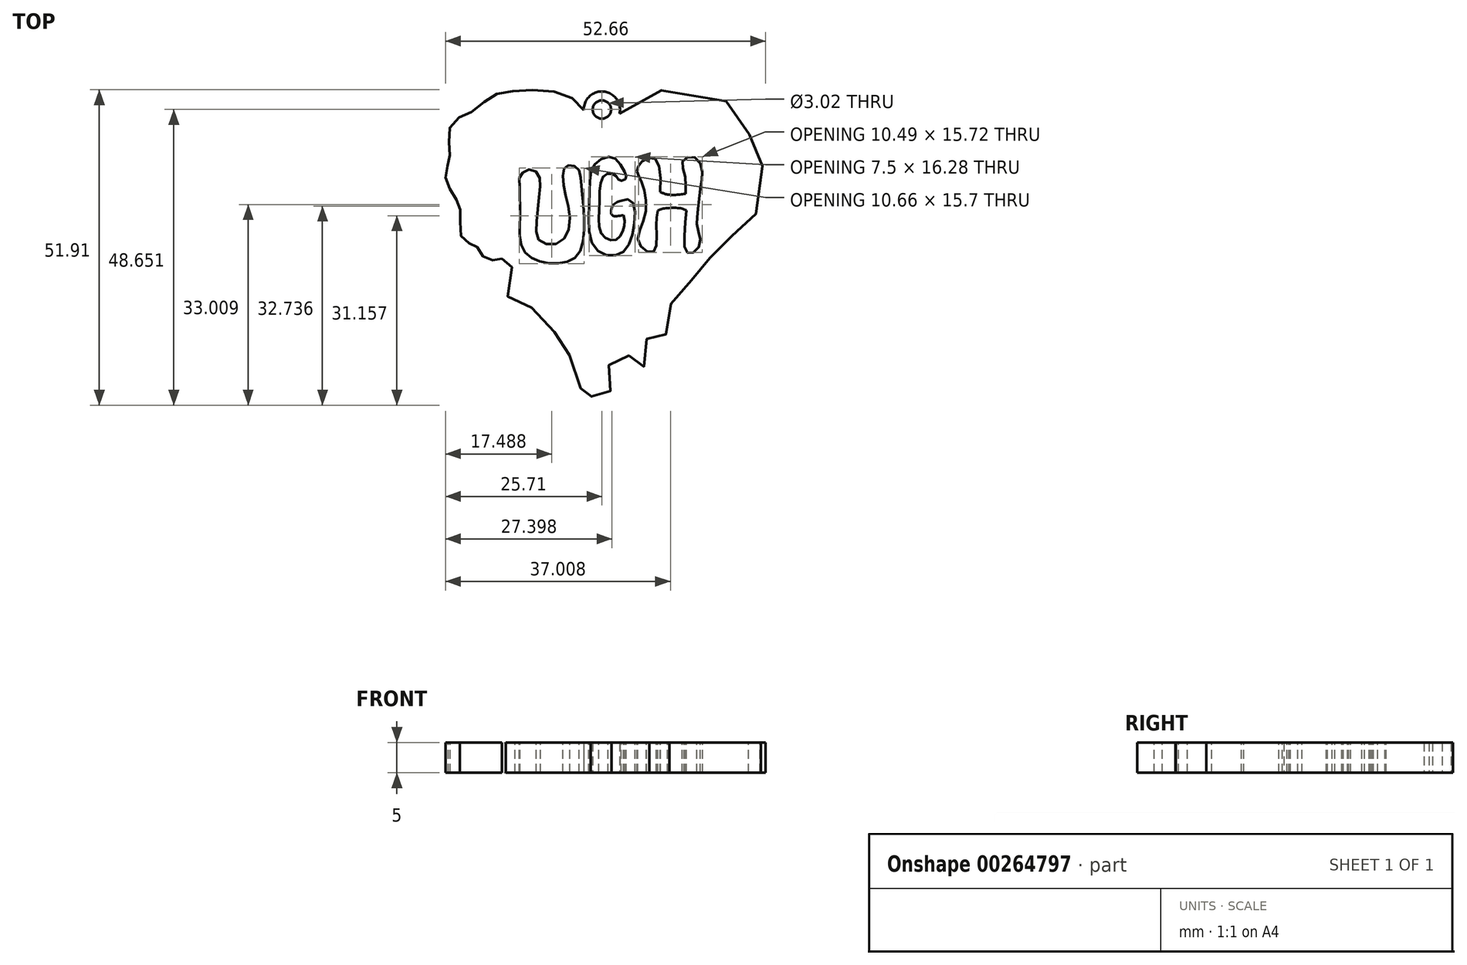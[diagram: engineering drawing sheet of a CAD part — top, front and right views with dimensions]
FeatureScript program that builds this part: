
annotation { "Feature Type Name" : "Feature", "Feature Type Description" : "" }
export const myFeature = defineFeature(function(context is Context, id is Id, definition is map)
    precondition{}
    {
        {
            var Q0;
            Q0=qCreatedBy(makeId("Top.planeOp"),FACE);
            var sketch = newSketch(context, id + "F0", { "sketchPlane" : qUnion([Q0])});
            skLineSegment(sketch, "E0", {"start": v(0.08, 15.96) * mm, "end": v(0.08, -29.04) * mm, "construction": true});
            skFitSpline(sketch, "E1", {"points": [v(0.08, 15.12) * mm, v(1.8, 15.96) * mm, v(5.58, 18.64) * mm, v(10.27, 20.57) * mm, v(19.75, 18.98) * mm, v(24.03, 15.96) * mm, v(24.45, 12.86) * mm, v(26.8, 11.1) * mm, v(26.13, 6.82) * mm, v(26.04, 2.12) * mm, v(23.27, -2.16) * mm, v(21.76, -2.5) * mm, v(21.1, -4.34) * mm, v(19.08, -6.1) * mm, v(17.82, -6.94) * mm, v(17.4, -9.03) * mm, v(15.64, -10.54) * mm, v(14.05, -10.96) * mm, v(13.55, -11.97) * mm, v(11.31, -14.7) * mm, v(10.84, -16.77) * mm, v(11.02, -19.08) * mm, v(9.42, -19.91) * mm, v(8.4, -19.08) * mm, v(7.52, -19.68) * mm, v(7.64, -22.23) * mm, v(7.7, -24.18) * mm, v(6.92, -24.96) * mm, v(6.21, -24.54) * mm, v(5.98, -25.01) * mm, v(5.09, -23.65) * mm, v(3.95, -23.12) * mm, v(3.15, -23.83) * mm, v(2.05, -24.06) * mm, v(1.07, -24.92) * mm, v(1.37, -27.18) * mm, v(1.6, -28.22) * mm, v(1.31, -29.31) * mm, v(0.68, -31) * mm, v(-1.46, -30.7) * mm, v(-1.93, -27.26) * mm, v(-2.64, -27.61) * mm, v(-3.35, -28.5) * mm, v(-4.3, -27.67) * mm, v(-5.2, -23.88) * mm, v(-5.67, -22.34) * mm, v(-6.74, -20.85) * mm, v(-7.62, -19.37) * mm, v(-10.41, -18.13) * mm, v(-11.48, -16) * mm, v(-12.13, -13.86) * mm, v(-14.5, -14.15) * mm, v(-15.75, -12.61) * mm, v(-15.51, -9.65) * mm, v(-15.04, -9) * mm, v(-14.33, -7.33) * mm, v(-14.5, -6.15) * mm, v(-16.46, -7.15) * mm], "startDerivative": vector(95.52, 38.59) * mm, "endDerivative": vector(-155.6, -97.2) * mm});
            skFitSpline(sketch, "E2", {"points": [v(-16.46, -7.15) * mm, v(-17.56, -7.42) * mm, v(-19.07, -7.15) * mm, v(-20.23, -5.85) * mm, v(-20.94, -4.84) * mm, v(-22.37, -4.47) * mm, v(-23.32, -2.82) * mm, v(-23.25, 0) * mm, v(-23.46, 1.56) * mm, v(-24.38, 3.32) * mm, v(-25.54, 5.33) * mm, v(-25.65, 7.1) * mm, v(-25.15, 9) * mm, v(-24.98, 10.83) * mm, v(-25.19, 13.83) * mm, v(-23.58, 15.97) * mm, v(-21.2, 17.06) * mm, v(-18.3, 19.45) * mm, v(-15.24, 20.33) * mm, v(-9.5, 20.5) * mm, v(-4.33, 18.86) * mm, v(-2.15, 16.14) * mm, v(-0.7, 15.1) * mm, v(0.08, 15.12) * mm], "startDerivative": vector(-33.79, -11.1) * mm, "endDerivative": vector(28.69, 5.55) * mm});
            skFitSpline(sketch, "E3", {"points": [v(-15.54, 7.18) * mm, v(-16.93, 6.43) * mm, v(-18.22, 6.03) * mm, v(-18.97, 4.49) * mm, v(-17.48, 2.5) * mm, v(-15.18, 1.6) * mm, v(-13.54, 0) * mm, v(-10.45, 0) * mm, v(-8.2, 0.55) * mm, v(-7.81, 0.5) * mm, v(-7.52, 0.56) * mm, v(-7.36, 1.37) * mm, v(-6.93, 1.67) * mm, v(-6.3, 2.5) * mm, v(-5.9, 2.96) * mm, v(-5.21, 3.13) * mm, v(-3.7, 4.49) * mm, v(-3.46, 7.08) * mm, v(-3.3, 9.72) * mm, v(-4.6, 11.37) * mm, v(-6.9, 10.92) * mm, v(-8.9, 8.87) * mm, v(-10.99, 8.82) * mm, v(-12.63, 8.57) * mm, v(-14.5, 8.18) * mm, v(-15.54, 7.18) * mm]});
            skFitSpline(sketch, "E4", {"points": [v(5.9, 10.84) * mm, v(4.72, 9.72) * mm, v(4.49, 8.06) * mm, v(5.44, 7.34) * mm, v(5.2, 5.8) * mm, v(6.27, 4.14) * mm, v(8.22, 3.6) * mm, v(9.82, 1.53) * mm, v(11.13, -0.54) * mm, v(12.61, -0.54) * mm, v(15.46, 1.06) * mm, v(17.47, 1.65) * mm, v(17.89, 4.2) * mm, v(15.93, 4.32) * mm, v(15.52, 7.17) * mm, v(14.92, 8.06) * mm, v(12.61, 8.47) * mm, v(11.25, 10.66) * mm, v(9.65, 10.66) * mm, v(6.86, 10.84) * mm, v(5.9, 10.84) * mm]});
            skCircle(sketch, "E5", {"center": v(0, 17.36) * mm, "radius": 2.97 * mm});
            skCircle(sketch, "E6", {"center": v(0, 17.36) * mm, "radius": 1.5 * mm});
            skSolve(sketch);
        }
        {
            var Q0;
            Q0=makeQuery(id+"F0.imprint","IMPRINT",FACE,{"disambiguationData":[TD([[makeQuery(id+"F0.imprint","IMPRINT",EDGE,{"derivedFrom":sQuery(id+"F0.wireOp",EDGE,"E1")}),-1.0]])]});
            var Q1;
            Q1=makeQuery(id+"F0.imprint","IMPRINT",FACE,{"disambiguationData":[TD([[makeQuery(id+"F0.imprint","IMPRINT",EDGE,{"derivedFrom":sQuery(id+"F0.wireOp",EDGE,"E3")}),-1.0]])]});
            var Q2;
            Q2=makeQuery(id+"F0.imprint","IMPRINT",FACE,{"disambiguationData":[TD([[makeQuery(id+"F0.imprint","IMPRINT",EDGE,{"derivedFrom":sQuery(id+"F0.wireOp",EDGE,"E6")}),-1.0]])]});
            var Q3;
            Q3=makeQuery(id+"F0.imprint","IMPRINT",FACE,{"disambiguationData":[TD([[makeQuery(id+"F0.imprint","IMPRINT",EDGE,{"derivedFrom":sQuery(id+"F0.wireOp",EDGE,"E3")}),1.0]])]});
            var Q4;
            Q4=makeQuery(id+"F0.imprint","IMPRINT",FACE,{"disambiguationData":[TD([[makeQuery(id+"F0.imprint","IMPRINT",EDGE,{"derivedFrom":sQuery(id+"F0.wireOp",EDGE,"E4")}),1.0]])]});
            extrude(context, id + "F1", {"entities" : qUnion([Q0, Q1, Q2, Q3, Q4]), "depth" : 5 * mm, "offsetDistance" : 25 * mm});
        }
        {
            var Q0;
            Q0=makeQuery(id+"F1.opExtrude","CAP_FACE",FACE,{"disambiguationData":[OSD([sQuery(id+"F0.wireOp",EDGE,"E1"),sQuery(id+"F0.wireOp",EDGE,"E2"),sQuery(id+"F0.wireOp",EDGE,"E5"),sQuery(id+"F0.wireOp",EDGE,"E6")])],"isStart":false});
            var sketch = newSketch(context, id + "F2", { "sketchPlane" : qUnion([Q0])});
            skFitSpline(sketch, "E7", {"points": [v(-13.55, 6.08) * mm, v(-13.47, 0) * mm, v(-12.81, -5.89) * mm, v(-8.17, -7.97) * mm, v(-3.71, -6.17) * mm, v(-3.14, 2.45) * mm, v(-3.77, 7.38) * mm], "startDerivative": vector(-0.58, -37.53) * mm, "endDerivative": vector(-7.1, 29.03) * mm});
            skFitSpline(sketch, "E8", {"points": [v(-13.55, 6.08) * mm, v(-12.76, 7.24) * mm, v(-11.25, 7.38) * mm, v(-10.2, 6.08) * mm, v(-10.3, 3.12) * mm, v(-10.73, -1.39) * mm, v(-10.44, -4.04) * mm, v(-7.93, -4.85) * mm, v(-5.7, -3.14) * mm, v(-5.42, 1.03) * mm, v(-6.27, 4.68) * mm, v(-6.32, 7.24) * mm, v(-5.8, 8.05) * mm, v(-4.67, 8.13) * mm, v(-3.77, 7.38) * mm], "startDerivative": vector(9.64, 12.64) * mm, "endDerivative": vector(9.45, -13.97) * mm});
            skFitSpline(sketch, "E9", {"points": [v(3.78, 7.08) * mm, v(1.63, 9.55) * mm, v(-1.32, 8.13) * mm, v(-2.04, 3.25) * mm, v(-1.24, -5.28) * mm, v(2.83, -6.47) * mm, v(5.22, -2.33) * mm, v(4.66, 2.45) * mm, v(2.75, 1.97) * mm, v(3.54, 0) * mm], "startDerivative": vector(-17.86, 33.71) * mm, "endDerivative": vector(14.27, -33.88) * mm});
            skFitSpline(sketch, "E10", {"points": [v(3.54, 0) * mm, v(3.54, -2.33) * mm, v(2.28, -4.1) * mm, v(0, -3.2) * mm, v(-0.4, 1.59) * mm, v(0.33, 6.46) * mm, v(2.1, 6.63) * mm, v(2.92, 5.68) * mm, v(3.94, 5.96) * mm, v(3.78, 7.08) * mm], "startDerivative": vector(7.5, -22.94) * mm, "endDerivative": vector(-6.57, 15.9) * mm});
            skFitSpline(sketch, "E11", {"points": [v(3.16, 2.36) * mm, v(1.77, 1.54) * mm, v(1.72, 0) * mm, v(3.54, 0) * mm], "startDerivative": vector(-4.9, -1.66) * mm, "endDerivative": vector(6.44, 1.48) * mm});
            skFitSpline(sketch, "E12", {"points": [v(5.82, 7.13) * mm, v(6.57, 5.39) * mm, v(7.13, 0) * mm, v(6.05, -4.54) * mm, v(8.49, -6.1) * mm, v(8.96, -1.72) * mm, v(9.36, 1.72) * mm, v(8.84, 9.16) * mm, v(6.5, 8.69) * mm, v(5.82, 7.13) * mm]});
            skFitSpline(sketch, "E13", {"points": [v(9.57, 3.8) * mm, v(10.85, 3.37) * mm, v(13.79, 3.5) * mm], "startDerivative": vector(3.2, -1.41) * mm, "endDerivative": vector(5.64, 0.94) * mm});
            skFitSpline(sketch, "E14", {"points": [v(9.21, 0.76) * mm, v(10.73, 1.14) * mm, v(13.3, 1.03) * mm, v(13.91, 0.76) * mm], "startDerivative": vector(3.88, 1.58) * mm, "endDerivative": vector(3.24, -0.62) * mm});
            skFitSpline(sketch, "E15", {"points": [v(15.22, 9.52) * mm, v(13.35, 8.97) * mm, v(13.68, 6.52) * mm, v(13.79, 3.5) * mm, v(13.91, 0.76) * mm, v(13.65, -5.4) * mm, v(14.58, -6.34) * mm, v(16.14, -4.82) * mm, v(15.7, -2.07) * mm, v(15.74, 0) * mm, v(16.17, 4.01) * mm, v(16.54, 7.21) * mm, v(15.22, 9.52) * mm]});
            skSolve(sketch);
        }
        {
            var Q0;
            Q0=makeQuery(id+"F2.imprint","IMPRINT",FACE,{"disambiguationData":[TD([[makeQuery(id+"F2.imprint","IMPRINT",EDGE,{"derivedFrom":sQuery(id+"F2.wireOp",EDGE,"E7")}),1.0]])]});
            var Q1;
            {var subQ0=sQuery(id+"F2.wireOp",EDGE,"E10");Q1=makeQuery(id+"F2.imprint","IMPRINT",FACE,{"disambiguationData":[TD([[makeQuery(id+"F2.imprint","IMPRINT",EDGE,{"derivedFrom":subQ0}),1.0]])]});}
            var Q2;
            {var subQ0=sQuery(id+"F2.wireOp",EDGE,"E11");Q2=makeQuery(id+"F2.imprint","IMPRINT",FACE,{"disambiguationData":[TD([[makeQuery(id+"F2.imprint","IMPRINT",EDGE,{"derivedFrom":subQ0}),1.0]])]});}
            var Q3;
            {var subQ0=sQuery(id+"F2.wireOp",EDGE,"E12");var subQ1=makeQuery(id+"F2.imprint","INTERSECT",VERTEX,{"derivedFrom":[subQ0,sQuery(id+"F2.wireOp",EDGE,"E13")]});Q3=makeQuery(id+"F2.imprint","IMPRINT",FACE,{"disambiguationData":[TD([[makeQuery(id+"F2.imprint","IMPRINT",EDGE,{"disambiguationData":[TD([[subQ1,1.0]])],"derivedFrom":subQ0}),1.0]])]});}
            var Q4;
            {var subQ0=sQuery(id+"F2.wireOp",EDGE,"E13");Q4=makeQuery(id+"F2.imprint","IMPRINT",FACE,{"disambiguationData":[TD([[makeQuery(id+"F2.imprint","IMPRINT",EDGE,{"derivedFrom":subQ0}),-1.0]])]});}
            var Q5;
            {var subQ0=sQuery(id+"F2.wireOp",EDGE,"E15");var subQ1=makeQuery(id+"F2.imprint","INTERSECT",VERTEX,{"derivedFrom":[sQuery(id+"F2.wireOp",EDGE,"E13"),subQ0]});Q5=makeQuery(id+"F2.imprint","IMPRINT",FACE,{"disambiguationData":[TD([[makeQuery(id+"F2.imprint","IMPRINT",EDGE,{"disambiguationData":[TD([[subQ1,-1.0]])],"derivedFrom":subQ0}),1.0]])]});}
            extrude(context, id + "F3", {"entities" : qUnion([Q0, Q1, Q2, Q3, Q4, Q5]), "operationType" : NewBodyOperationType.REMOVE, "oppositeDirection" : true, "depth" : 25 * mm, "offsetDistance" : 25 * mm});
        }
    });
